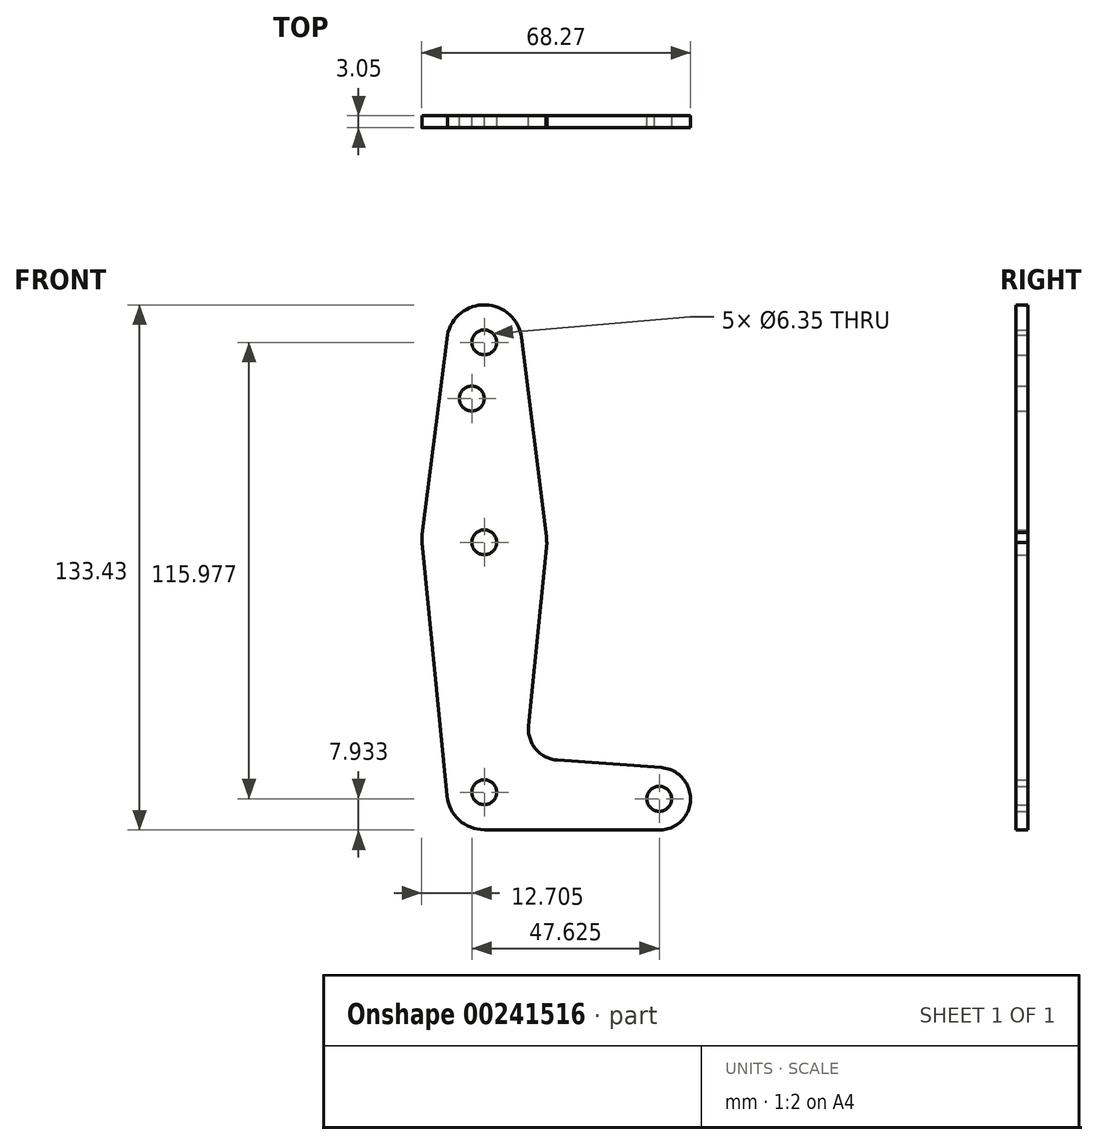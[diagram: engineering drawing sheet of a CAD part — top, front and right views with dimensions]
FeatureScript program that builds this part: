
annotation { "Feature Type Name" : "Feature", "Feature Type Description" : "" }
export const myFeature = defineFeature(function(context is Context, id is Id, definition is map)
    precondition{}
    {
        {
            var Q0;
            Q0=qCreatedBy(makeId("Front.planeOp"),FACE);
            var sketch = newSketch(context, id + "F0", { "sketchPlane" : qUnion([Q0])});
            skCircle(sketch, "E0", {"center": v(0, 0) * mm, "radius": 15.87 * mm});
            skCircle(sketch, "E1", {"center": v(0, 50.8) * mm, "radius": 9.53 * mm});
            skCircle(sketch, "E2", {"center": v(0, -63.5) * mm, "radius": 9.53 * mm});
            skCircle(sketch, "E3", {"center": v(44.45, -65.18) * mm, "radius": 7.94 * mm});
            skLineSegment(sketch, "E4", {"start": v(-9.35, 52.61) * mm, "end": v(-15.75, 2) * mm});
            skLineSegment(sketch, "E5", {"start": v(-15.87, 0) * mm, "end": v(-9.48, -64.44) * mm});
            skLineSegment(sketch, "E6", {"start": v(15.68, 2.46) * mm, "end": v(9.45, 51.99) * mm});
            skLineSegment(sketch, "E7", {"start": v(15.87, 0) * mm, "end": v(11.25, -46.62) * mm});
            skLineSegment(sketch, "E8", {"start": v(18.58, -55.33) * mm, "end": v(45.03, -57.26) * mm});
            skLineSegment(sketch, "E9", {"start": v(0, -73.03) * mm, "end": v(45.64, -73.03) * mm});
            skCircle(sketch, "E10", {"center": v(-3.18, 36.53) * mm, "radius": 3.18 * mm});
            skCircle(sketch, "E11", {"center": v(0, 50.8) * mm, "radius": 3.18 * mm});
            skCircle(sketch, "E12", {"center": v(0, 0) * mm, "radius": 3.18 * mm});
            skCircle(sketch, "E13", {"center": v(0, -63.5) * mm, "radius": 3.18 * mm});
            skCircle(sketch, "E14", {"center": v(44.45, -65.18) * mm, "radius": 3.18 * mm});
            skPoint(sketch, "E15.newPointB", {"position": v(0, -53.98) * mm});
            skArc(sketch, "E15.filletArc", {"start": v(11.25, -46.62) * mm, "mid": v(13.08, -52.52) * mm, "end": v(18.58, -55.33) * mm});
            skSolve(sketch);
        }
        {
            var Q0;
            {var subQ0=sQuery(id+"F0.wireOp",EDGE,"E5");var subQ1=sQuery(id+"F0.wireOp",EDGE,"E0");var subQ2=makeQuery(id+"F0.imprint","INTERSECT",VERTEX,{"disambiguationData":[OD(0.0)],"derivedFrom":[subQ1,subQ0]});Q0=makeQuery(id+"F0.imprint","IMPRINT",FACE,{"disambiguationData":[TD([[makeQuery(id+"F0.imprint","IMPRINT",EDGE,{"disambiguationData":[TD([[subQ2,-1.0]])],"derivedFrom":subQ1}),1.0]])]});}
            var Q1;
            {var subQ0=sQuery(id+"F0.wireOp",EDGE,"E7");var subQ1=sQuery(id+"F0.wireOp",EDGE,"E0");var subQ2=makeQuery(id+"F0.imprint","INTERSECT",VERTEX,{"disambiguationData":[OD(0.0)],"derivedFrom":[subQ1,subQ0]});Q1=makeQuery(id+"F0.imprint","IMPRINT",FACE,{"disambiguationData":[TD([[makeQuery(id+"F0.imprint","IMPRINT",EDGE,{"disambiguationData":[TD([[subQ2,1.0]])],"derivedFrom":subQ1}),1.0]])]});}
            var Q2;
            {var subQ0=sQuery(id+"F0.wireOp",EDGE,"E4");var subQ1=sQuery(id+"F0.wireOp",EDGE,"E1");var subQ2=makeQuery(id+"F0.imprint","INTERSECT",VERTEX,{"disambiguationData":[OD(0.0)],"derivedFrom":[subQ1,subQ0]});Q2=makeQuery(id+"F0.imprint","IMPRINT",FACE,{"disambiguationData":[TD([[makeQuery(id+"F0.imprint","IMPRINT",EDGE,{"disambiguationData":[TD([[subQ2,-1.0]])],"derivedFrom":subQ1}),1.0]])]});}
            var Q3;
            {var subQ0=sQuery(id+"F0.wireOp",EDGE,"E9");var subQ1=sQuery(id+"F0.wireOp",EDGE,"E3");var subQ2=makeQuery(id+"F0.imprint","INTERSECT",VERTEX,{"disambiguationData":[OD(0.0)],"derivedFrom":[subQ1,subQ0]});Q3=makeQuery(id+"F0.imprint","IMPRINT",FACE,{"disambiguationData":[TD([[makeQuery(id+"F0.imprint","IMPRINT",EDGE,{"disambiguationData":[TD([[subQ2,1.0]])],"derivedFrom":subQ1}),1.0]])]});}
            var Q4;
            Q4=makeQuery(id+"F0.imprint","IMPRINT",FACE,{"disambiguationData":[TD([[makeQuery(id+"F0.imprint","IMPRINT",EDGE,{"derivedFrom":sQuery(id+"F0.wireOp",EDGE,"E13")}),-1.0]])]});
            var Q5;
            {var subQ5=sQuery(id+"F0.wireOp",EDGE,"E8");Q5=makeQuery(id+"F0.imprint","IMPRINT",FACE,{"disambiguationData":[TD([[makeQuery(id+"F0.imprint","IMPRINT",EDGE,{"derivedFrom":subQ5}),-1.0]])]});}
            var Q6;
            Q6=makeQuery(id+"F0.imprint","IMPRINT",FACE,{"disambiguationData":[TD([[makeQuery(id+"F0.imprint","IMPRINT",EDGE,{"derivedFrom":sQuery(id+"F0.wireOp",EDGE,"E11")}),-1.0]])]});
            var Q7;
            Q7=makeQuery(id+"F0.imprint","IMPRINT",FACE,{"disambiguationData":[TD([[makeQuery(id+"F0.imprint","IMPRINT",EDGE,{"derivedFrom":sQuery(id+"F0.wireOp",EDGE,"E14")}),-1.0]])]});
            var Q8;
            Q8=makeQuery(id+"F0.imprint","IMPRINT",FACE,{"disambiguationData":[TD([[makeQuery(id+"F0.imprint","IMPRINT",EDGE,{"derivedFrom":sQuery(id+"F0.wireOp",EDGE,"E12")}),-1.0]])]});
            var Q9;
            {var subQ5=sQuery(id+"F0.wireOp",EDGE,"E6");Q9=makeQuery(id+"F0.imprint","IMPRINT",FACE,{"disambiguationData":[TD([[makeQuery(id+"F0.imprint","IMPRINT",EDGE,{"derivedFrom":subQ5}),1.0]])]});}
            extrude(context, id + "F1", {"entities" : qUnion([Q0, Q1, Q2, Q3, Q4, Q5, Q6, Q7, Q8, Q9]), "depth" : 3.05 * mm});
        }
    });
